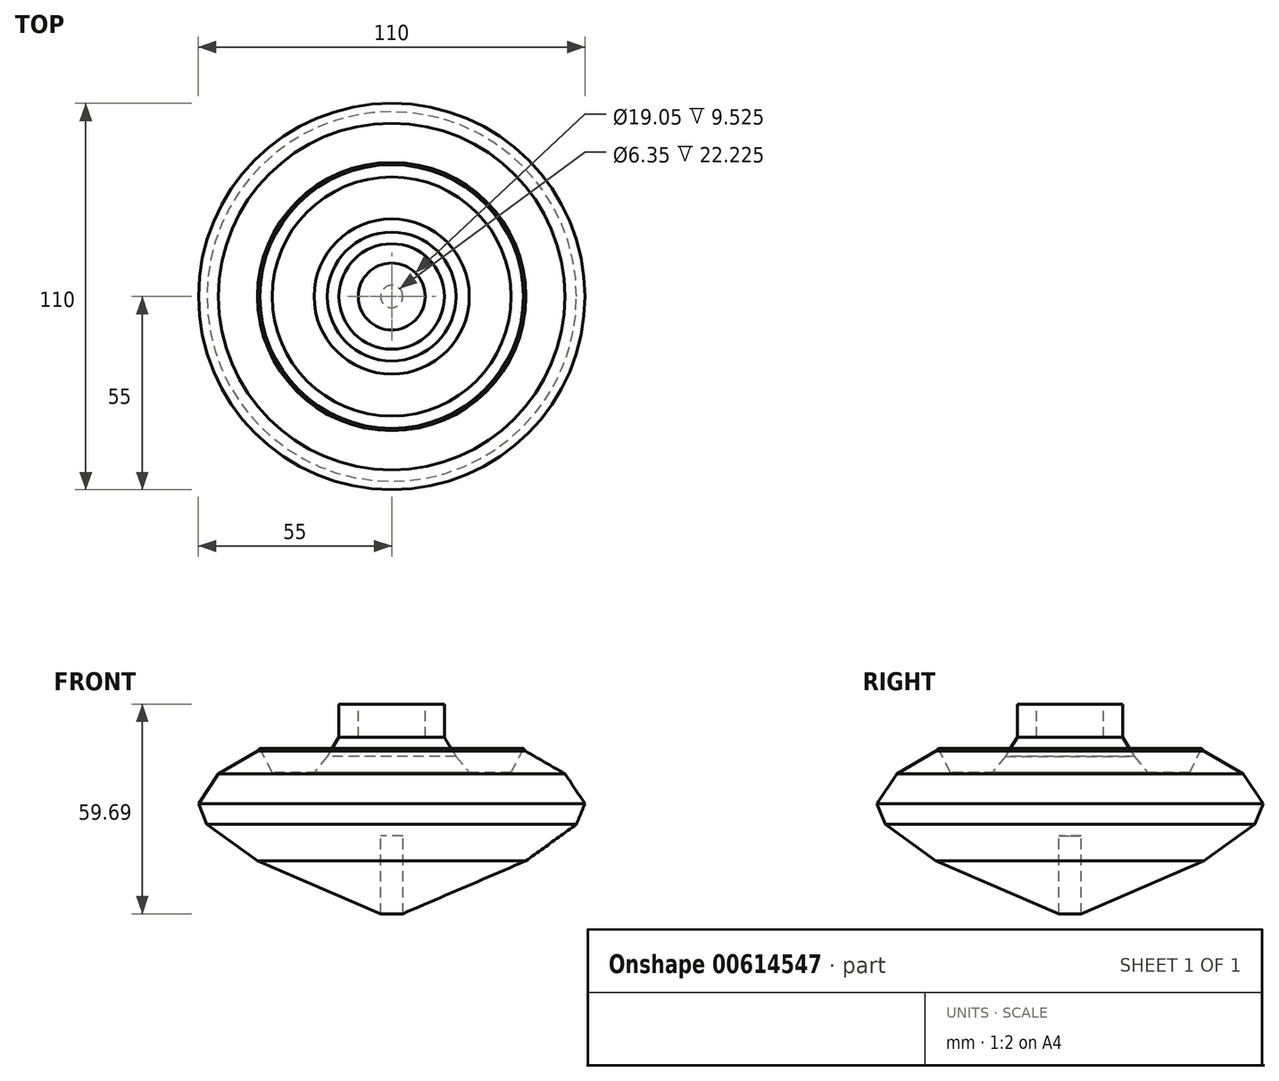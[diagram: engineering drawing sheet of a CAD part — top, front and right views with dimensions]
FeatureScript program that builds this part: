
annotation { "Feature Type Name" : "Feature", "Feature Type Description" : "" }
export const myFeature = defineFeature(function(context is Context, id is Id, definition is map)
    precondition{}
    {
        {
            var Q0;
            Q0=qCreatedBy(makeId("Front.planeOp"),FACE);
            var sketch = newSketch(context, id + "F0", { "sketchPlane" : qUnion([Q0])});
            skLineSegment(sketch, "E0", {"start": v(0, 22.22) * mm, "end": v(3.18, 22.22) * mm});
            skLineSegment(sketch, "E1", {"start": v(3.18, 22.22) * mm, "end": v(3.18, 0) * mm});
            skLineSegment(sketch, "E2", {"start": v(3.18, 0) * mm, "end": v(38.18, 15.05) * mm});
            skLineSegment(sketch, "E3", {"start": v(38.18, 15.05) * mm, "end": v(52.6, 25.46) * mm});
            skLineSegment(sketch, "E4", {"start": v(52.6, 25.46) * mm, "end": v(55, 31.33) * mm});
            skLineSegment(sketch, "E5", {"start": v(55, 31.33) * mm, "end": v(49.32, 39.84) * mm});
            skLineSegment(sketch, "E6", {"start": v(49.32, 39.84) * mm, "end": v(38.18, 46.25) * mm});
            skLineSegment(sketch, "E7", {"start": v(38.18, 46.25) * mm, "end": v(37.51, 47.02) * mm});
            skLineSegment(sketch, "E8", {"start": v(37.51, 47.02) * mm, "end": v(34.02, 40.25) * mm});
            skLineSegment(sketch, "E9", {"start": v(34.02, 40.25) * mm, "end": v(26.4, 40.25) * mm});
            skLineSegment(sketch, "E10", {"start": v(9.53, 59.7) * mm, "end": v(9.53, 50.17) * mm});
            skLineSegment(sketch, "E11", {"start": v(9.53, 50.17) * mm, "end": v(0, 50.17) * mm});
            skLineSegment(sketch, "E12", {"start": v(0, 50.17) * mm, "end": v(0, 22.22) * mm});
            skLineSegment(sketch, "E13", {"start": v(9.53, 59.7) * mm, "end": v(15, 59.7) * mm});
            skLineSegment(sketch, "E14", {"start": v(15, 59.7) * mm, "end": v(15, 50.21) * mm});
            skLineSegment(sketch, "E15", {"start": v(15, 50.21) * mm, "end": v(18.34, 44.8) * mm});
            skLineSegment(sketch, "E16", {"start": v(18.34, 44.8) * mm, "end": v(22.09, 40.25) * mm});
            skLineSegment(sketch, "E17", {"start": v(22.09, 40.25) * mm, "end": v(26.4, 40.25) * mm});
            skSolve(sketch);
        }
        {
            var Q0;
            Q0=makeQuery(id+"F0.imprint","IMPRINT",FACE,{"disambiguationData":[TD([[makeQuery(id+"F0.imprint","IMPRINT",EDGE,{"derivedFrom":sQuery(id+"F0.wireOp",EDGE,"E0")}),1.0]])]});
            var Q1;
            Q1=sQuery(id+"F0.wireOp",EDGE,"E12");
            revolve(context, id + "F1", {"entities" : qUnion([Q0]), "axis" : qUnion([Q1]), "revolveType" : RevolveType.FULL});
        }
    });
